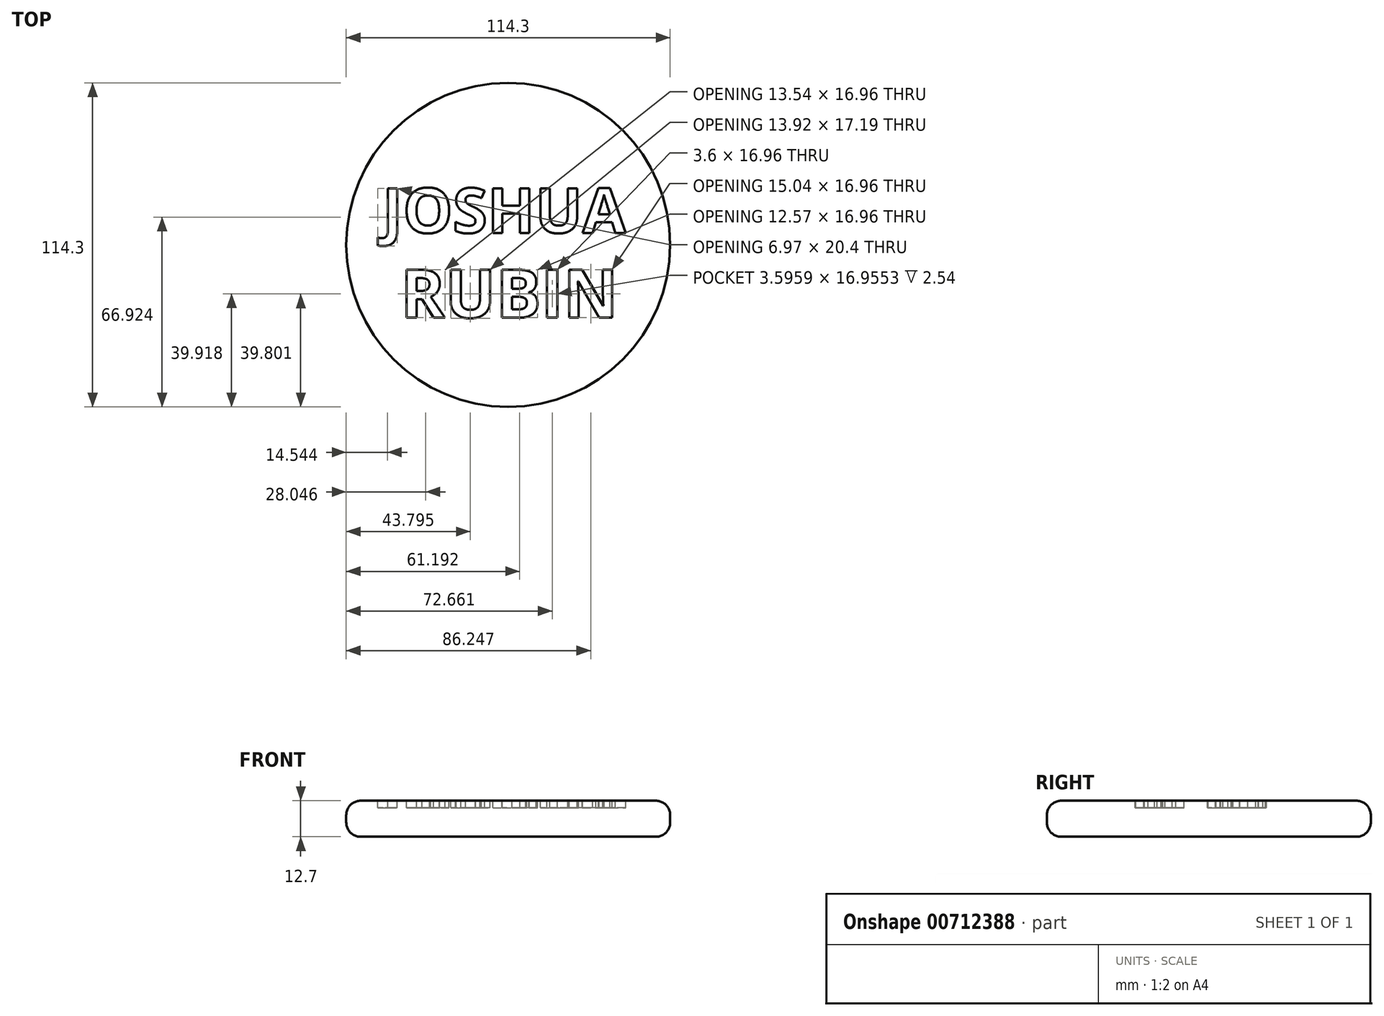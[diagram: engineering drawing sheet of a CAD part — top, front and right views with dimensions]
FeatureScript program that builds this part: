
annotation { "Feature Type Name" : "Feature", "Feature Type Description" : "" }
export const myFeature = defineFeature(function(context is Context, id is Id, definition is map)
    precondition{}
    {
        {
            var Q0;
            Q0=qCreatedBy(makeId("Top.planeOp"),FACE);
            var sketch = newSketch(context, id + "F0", { "sketchPlane" : qUnion([Q0])});
            skCircle(sketch, "E0", {"center": v(0, 0) * mm, "radius": 57.15 * mm});
            skSolve(sketch);
        }
        {
            var Q0;
            Q0 = qSketchRegion(id + "F0", true);
            extrude(context, id + "F1", {"entities" : qUnion([Q0]), "depth" : 12.7 * mm, "offsetDistance" : 25.4 * mm});
        }
        {
            var Q0;
            Q0=makeQuery(id+"F1.opExtrude","CAP_EDGE",EDGE,{"disambiguationData":[OSD([sQuery(id+"F0.wireOp",EDGE,"E0")])],"isStart":false});
            var Q1;
            Q1=makeQuery(id+"F1.opExtrude","CAP_EDGE",EDGE,{"disambiguationData":[OSD([sQuery(id+"F0.wireOp",EDGE,"E0")])],"isStart":true});
            fillet(context, id + "F2", {"entities" : qUnion([Q0, Q1]), "radius" : 5.08 * mm, "tangentPropagation" : true, "allowEdgeOverflow" : false});
        }
        {
            var Q0;
            Q0=makeQuery(id+"F1.opExtrude","CAP_FACE",FACE,{"disambiguationData":[OSD([sQuery(id+"F0.wireOp",EDGE,"E0")])],"isStart":false});
            var sketch = newSketch(context, id + "F3", { "sketchPlane" : qUnion([Q0])});
            skText(sketch, "E1", { "text": "JOSHUA", "fontName": "OpenSans-Bold.ttf"});
            skLineSegment(sketch, "E2", {"start": v(0, 52.07) * mm, "end": v(0, -52.07) * mm, "construction": true});
            skPoint(sketch, "E3.endSnap0", {"position": v(-44.45, 12.16) * mm});
            skLineSegment(sketch, "E4", {"start": v(-50.63, 12.16) * mm, "end": v(50.63, 12.16) * mm, "construction": true});
            skLineSegment(sketch, "E5", {"start": v(0, 20.1) * mm, "end": v(0, 4.21) * mm, "construction": true});
            skText(sketch, "E6", { "text": "RUBIN", "fontName": "OpenSans-Bold.ttf"});
            skLineSegment(sketch, "E7", {"start": v(0.09, -8.6) * mm, "end": v(0.09, -25.71) * mm, "construction": true});
            skPoint(sketch, "E8", {"position": v(0, 12.16) * mm});
            const initialGuessF3  = {"E1": [-0.04445, 0.00421, 1, 0, 0.0159], "E6": [-0.03801, -0.02571, 1, 0, 0.0171]};
            skSetInitialGuess(sketch, initialGuessF3);
            skSolve(sketch);
        }
        {
            var Q0;
            Q0 = qSketchRegion(id + "F3", true);
            extrude(context, id + "F4", {"entities" : qUnion([Q0]), "operationType" : NewBodyOperationType.REMOVE, "oppositeDirection" : true, "depth" : 2.54 * mm, "offsetDistance" : 25.4 * mm});
        }
    });
